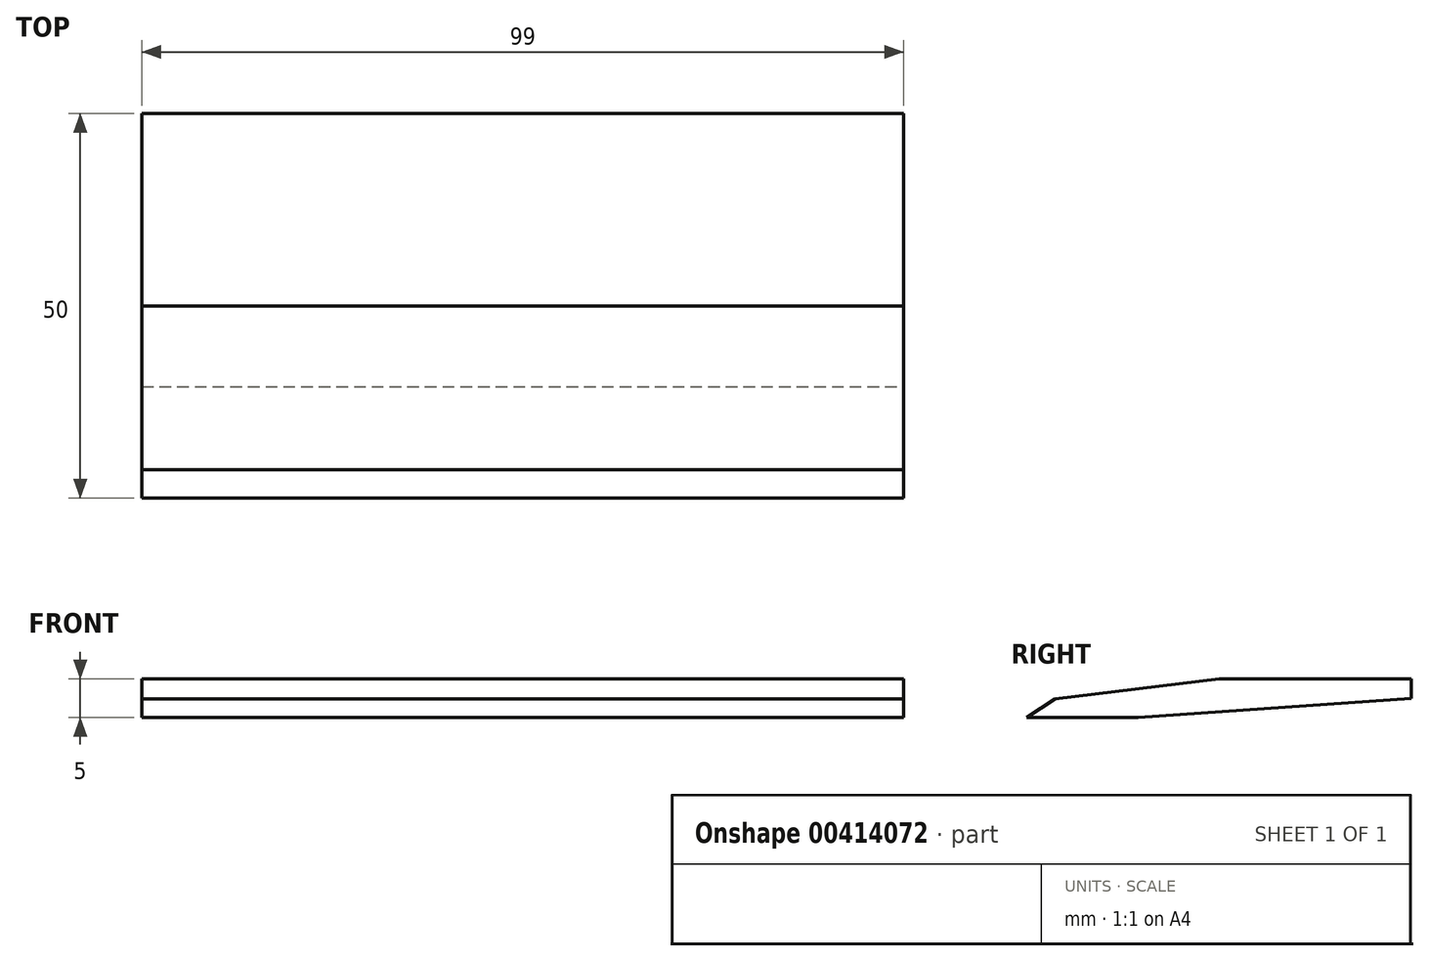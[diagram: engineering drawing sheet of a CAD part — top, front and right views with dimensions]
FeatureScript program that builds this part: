
annotation { "Feature Type Name" : "Feature", "Feature Type Description" : "" }
export const myFeature = defineFeature(function(context is Context, id is Id, definition is map)
    precondition{}
    {
        {
            var Q0;
            Q0=qCreatedBy(makeId("Top.planeOp"),FACE);
            var sketch = newSketch(context, id + "F0", { "sketchPlane" : qUnion([Q0])});
            skLineSegment(sketch, "E0.bottom", {"start": v(49.5, -25) * mm, "end": v(-49.5, -25) * mm});
            skLineSegment(sketch, "E0.top", {"start": v(49.5, 25) * mm, "end": v(-49.5, 25) * mm});
            skLineSegment(sketch, "E0.left", {"start": v(49.5, -25) * mm, "end": v(49.5, 25) * mm});
            skLineSegment(sketch, "E0.right", {"start": v(-49.5, -25) * mm, "end": v(-49.5, 25) * mm});
            skPoint(sketch, "E0.middle", {"position": v(0, 0) * mm});
            skSolve(sketch);
        }
        {
            var Q0;
            Q0=makeQuery(id+"F0.imprint","IMPRINT",FACE,{"disambiguationData":[TD([[makeQuery(id+"F0.imprint","IMPRINT",EDGE,{"derivedFrom":sQuery(id+"F0.wireOp",EDGE,"E0.bottom")}),-1.0]])]});
            extrude(context, id + "F1", {"entities" : qUnion([Q0]), "depth" : 5 * mm});
        }
        {
            var Q0;
            Q0=makeQuery(id+"F1.opExtrude","SWEPT_FACE",FACE,{"disambiguationData":[OSD([sQuery(id+"F0.wireOp",EDGE,"E0.left")])]});
            var sketch = newSketch(context, id + "F2", { "sketchPlane" : qUnion([Q0])});
            skLineSegment(sketch, "E1", {"start": v(0, 5) * mm, "end": v(0, 0) * mm});
            skLineSegment(sketch, "E2", {"start": v(0, 5) * mm, "end": v(-21.32, 2.41) * mm});
            skLineSegment(sketch, "E3", {"start": v(-21.32, 2.41) * mm, "end": v(-25, 0) * mm});
            skSolve(sketch);
        }
        {
            var Q0;
            {var subQ0=sQuery(id+"F2.wireOp",EDGE,"E2");Q0=makeQuery(id+"F2.imprint","IMPRINT",FACE,{"disambiguationData":[TD([[makeQuery(id+"F2.imprint","IMPRINT",EDGE,{"derivedFrom":subQ0}),-1.0]])]});}
            extrude(context, id + "F3", {"entities" : qUnion([Q0]), "operationType" : NewBodyOperationType.REMOVE, "oppositeDirection" : true, "depth" : 127 * mm});
        }
        {
            var Q0;
            Q0=makeQuery(id+"F1.opExtrude","SWEPT_FACE",FACE,{"disambiguationData":[OSD([sQuery(id+"F0.wireOp",EDGE,"E0.left")])]});
            var sketch = newSketch(context, id + "F4", { "sketchPlane" : qUnion([Q0])});
            skLineSegment(sketch, "E4", {"start": v(-10.52, 0) * mm, "end": v(25, 2.5) * mm});
            skLineSegment(sketch, "E5", {"start": v(25, 2.5) * mm, "end": v(25, 5) * mm});
            skLineSegment(sketch, "E6", {"start": v(25, 5) * mm, "end": v(0, 5) * mm});
            skLineSegment(sketch, "E7", {"start": v(0, 5) * mm, "end": v(-21.32, 2.41) * mm});
            skLineSegment(sketch, "E8", {"start": v(-21.32, 2.41) * mm, "end": v(-25, 0) * mm});
            skLineSegment(sketch, "E9", {"start": v(-25, 0) * mm, "end": v(-10.52, 0) * mm});
            skLineSegment(sketch, "E10", {"start": v(25, 2.5) * mm, "end": v(25, 0) * mm});
            skLineSegment(sketch, "E11", {"start": v(25, 0) * mm, "end": v(-10.52, 0) * mm});
            skSolve(sketch);
        }
        {
            var Q0;
            Q0=makeQuery(id+"F4.imprint","IMPRINT",FACE,{"disambiguationData":[TD([[makeQuery(id+"F4.imprint","IMPRINT",EDGE,{"derivedFrom":sQuery(id+"F4.wireOp",EDGE,"E4")}),-1.0]])]});
            extrude(context, id + "F5", {"entities" : qUnion([Q0]), "operationType" : NewBodyOperationType.REMOVE, "oppositeDirection" : true, "depth" : 152.4 * mm});
        }
    });
